annotation { "Feature Type Name" : "Feature", "Feature Type Description" : "" }
export const myFeature = defineFeature(function(context is Context, id is Id, definition is map)
    precondition{}
    {
        {
            var Q0;
            Q0=qCreatedBy(makeId("Top.planeOp"),FACE);
            var sketch = newSketch(context, id + "F0", { "sketchPlane" : qUnion([Q0])});
            skFitSpline(sketch, "E0", {"points": [v(57.34, 19.53) * mm, v(62.96, 14.6) * mm, v(65.23, 11.51) * mm, v(65.1, 6.78) * mm, v(63.4, 0.47) * mm, v(62.01, -6.29) * mm, v(62.2, -11.34) * mm, v(63.15, -16.32) * mm, v(62.96, -19.92) * mm, v(60.37, -26.55) * mm, v(57.34, -32.42) * mm, v(54.19, -36.9) * mm, v(51.85, -41.58) * mm, v(52.1, -45.11) * mm, v(51.79, -48.9) * mm, v(50.34, -52.24) * mm, v(46.61, -58.37) * mm, v(45.8, -61.9) * mm, v(44.84, -66.64) * mm, v(41.94, -71.18) * mm, v(36.83, -74.46) * mm, v(29.95, -76.36) * mm, v(24.45, -76.86) * mm, v(21.55, -76.17) * mm, v(19.21, -76.42) * mm, v(15.55, -77.12) * mm, v(11, -77.75) * mm, v(1.73, -77.87) * mm, v(-11.34, -73.7) * mm, v(-18.1, -68.47) * mm, v(-21.38, -62.85) * mm, v(-23.27, -59.63) * mm, v(-27.18, -57.42) * mm, v(-33.56, -52.18) * mm, v(-39.3, -44.92) * mm, v(-42.2, -35.52) * mm, v(-42.33, -35.45) * mm, v(-44.16, -36.02) * mm, v(-47.45, -35.2) * mm, v(-49.34, -32.42) * mm, v(-50.29, -26.49) * mm, v(-50.16, -22.57) * mm, v(-51.42, -17.4) * mm, v(-51.42, -15.44) * mm, v(-54.96, -10.26) * mm, v(-57.04, -5.85) * mm, v(-57.48, -1.17) * mm, v(-56.28, 4.5) * mm, v(-58.18, 7.85) * mm, v(-59.7, 15.05) * mm, v(-59.95, 22.3) * mm, v(-59.44, 34.18) * mm, v(-60.26, 40.87) * mm, v(-53.82, 51.28) * mm, v(-48.65, 57.6) * mm, v(-42.52, 64.22) * mm, v(-33.69, 70.73) * mm, v(-24.6, 75.27) * mm, v(-12.54, 78.55) * mm, v(1.8, 79.7) * mm, v(18.4, 77.92) * mm, v(39.16, 72.05) * mm, v(51.1, 64.67) * mm, v(56.9, 57.85) * mm, v(59.1, 48.95) * mm, v(59.3, 45.16) * mm, v(56.71, 42.07) * mm, v(54.31, 41.56) * mm, v(51.91, 41.69) * mm, v(52.1, 38.22) * mm, v(54.5, 31.84) * mm, v(56.02, 23.82) * mm, v(57.34, 19.53) * mm]});
            skSolve(sketch);
        }
        {
            var Q0;
            Q0 = qSketchRegion(id + "F0", true);
            extrude(context, id + "F1", {"entities" : qUnion([Q0]), "oppositeDirection" : true, "depth" : 6.35 * mm, "offsetDistance" : 25.4 * mm});
        }
        {
            var Q0;
            Q0=qCreatedBy(makeId("Top.planeOp"),FACE);
            var sketch = newSketch(context, id + "F2", { "sketchPlane" : qUnion([Q0])});
            skFitSpline(sketch, "E1", {"points": [v(-27.86, 37.73) * mm, v(-24.64, 35.15) * mm, v(-22.36, 34.68) * mm, v(-20.83, 36.15) * mm, v(-20.77, 37.61) * mm, v(-23.18, 41.13) * mm, v(-28.27, 46.87) * mm, v(-30.09, 48.4) * mm, v(-31.5, 48.74) * mm, v(-34.01, 46.75) * mm, v(-34.13, 44) * mm, v(-32.96, 42.65) * mm, v(-27.86, 37.73) * mm]});
            skFitSpline(sketch, "E2", {"points": [v(-23, 44.4) * mm, v(-21.71, 41.6) * mm, v(-20.01, 39.6) * mm, v(-17.73, 39.25) * mm, v(-15.62, 40.2) * mm, v(-15.15, 41.89) * mm, v(-16.67, 46.87) * mm, v(-18.78, 53.02) * mm, v(-20.36, 56.48) * mm, v(-22.47, 57.77) * mm, v(-26.46, 56.71) * mm, v(-27.92, 54.54) * mm, v(-27.69, 52.32) * mm, v(-26.16, 49.33) * mm, v(-23, 44.4) * mm]});
            skFitSpline(sketch, "E3", {"points": [v(-17.55, 55.3) * mm, v(-18.25, 57.77) * mm, v(-17.26, 59.46) * mm, v(-14.39, 60.4) * mm, v(-11.7, 59.35) * mm, v(-10.4, 56.6) * mm, v(-9.35, 50.91) * mm, v(-8.65, 45.81) * mm, v(-9.64, 43.12) * mm, v(-11.28, 42.7) * mm, v(-13.8, 43.88) * mm, v(-14.86, 46.17) * mm, v(-16.67, 51.97) * mm, v(-17.55, 55.3) * mm]});
            skFitSpline(sketch, "E4", {"points": [v(-7.36, 54.49) * mm, v(-6.89, 60.17) * mm, v(-6.36, 62.22) * mm, v(-4.84, 62.51) * mm, v(-3.08, 61.28) * mm, v(-1.32, 59.82) * mm, v(-0.33, 58.53) * mm, v(-0.5, 54.9) * mm, v(-0.21, 50.2) * mm, v(-0.15, 44.76) * mm, v(-0.1, 42.07) * mm, v(-0.62, 42.07) * mm, v(-4.02, 42.65) * mm, v(-6.07, 44.17) * mm, v(-6.71, 46.87) * mm, v(-7.12, 52.2) * mm, v(-7.36, 54.49) * mm]});
            skFitSpline(sketch, "E5", {"points": [v(2.2, 49.1) * mm, v(2.78, 53.14) * mm, v(2.95, 57.41) * mm, v(3.42, 59.82) * mm, v(4.53, 60.46) * mm, v(7.23, 59.58) * mm, v(9.1, 58.23) * mm, v(9.98, 55.36) * mm, v(9.63, 48.98) * mm, v(8.87, 42.53) * mm, v(8.46, 39.84) * mm, v(6.7, 39.49) * mm, v(3.71, 41.36) * mm, v(2.3, 43.88) * mm, v(2.2, 49.1) * mm]});
            skFitSpline(sketch, "E6", {"points": [v(12.38, 42.65) * mm, v(11.8, 49.8) * mm, v(12.15, 54.37) * mm, v(13.03, 56.95) * mm, v(15.43, 58.7) * mm, v(17.13, 58.3) * mm, v(18.42, 56.6) * mm, v(18.65, 54.6) * mm, v(18.65, 51.09) * mm, v(18.83, 47.63) * mm, v(18.89, 43.94) * mm, v(18.71, 40.13) * mm, v(18.65, 36.68) * mm, v(18.36, 35.27) * mm, v(17.42, 34.8) * mm, v(15.9, 35.04) * mm, v(13.38, 36.68) * mm, v(12.74, 38.55) * mm, v(12.38, 42.65) * mm]});
            skFitSpline(sketch, "E7", {"points": [v(25.62, 40.72) * mm, v(23.75, 37.79) * mm, v(22.4, 37.73) * mm, v(21.46, 40.72) * mm, v(20.88, 47.75) * mm, v(21.4, 54.3) * mm, v(22.87, 58.18) * mm, v(24.86, 59.23) * mm, v(27.44, 58.59) * mm, v(27.62, 56.83) * mm, v(27.67, 52.38) * mm, v(27.26, 46.87) * mm, v(26.97, 42.6) * mm, v(25.62, 40.72) * mm]});
            skFitSpline(sketch, "E8", {"points": [v(29.78, 51.44) * mm, v(29.55, 48.1) * mm, v(30.2, 45.35) * mm, v(31.83, 45.58) * mm, v(34.53, 46.4) * mm, v(35.35, 48.98) * mm, v(36.46, 53.78) * mm, v(36.99, 57) * mm, v(35.17, 58.64) * mm, v(33.06, 58.88) * mm, v(30.84, 57.82) * mm, v(30.37, 54.78) * mm, v(29.78, 51.44) * mm]});
            skFitSpline(sketch, "E9", {"points": [v(36.76, 48.28) * mm, v(38.51, 52.61) * mm, v(40.45, 55.72) * mm, v(42.09, 56.36) * mm, v(44.14, 55.19) * mm, v(44.25, 53.37) * mm, v(42.79, 49.74) * mm, v(40.45, 46.4) * mm, v(39.8, 44.88) * mm, v(37.87, 44.64) * mm, v(36.76, 48.28) * mm]});
            skFitSpline(sketch, "E10", {"points": [v(43.08, 42.89) * mm, v(42.26, 44.35) * mm, v(43.5, 46.87) * mm, v(45.95, 51.26) * mm, v(46.83, 53.55) * mm, v(49.23, 53.72) * mm, v(50.4, 51.09) * mm, v(49.94, 48.22) * mm, v(48.06, 45) * mm, v(45.66, 42.24) * mm, v(44.2, 41.6) * mm, v(43.08, 42.89) * mm]});
            skFitSpline(sketch, "E11", {"points": [v(-41.16, 32.22) * mm, v(-39.64, 35.33) * mm, v(-37.18, 37.09) * mm, v(-33.49, 36.91) * mm, v(-28.16, 36.09) * mm, v(-25.58, 34.86) * mm, v(-25.34, 33.16) * mm, v(-26.8, 29.76) * mm, v(-28.98, 28.7) * mm, v(-31.79, 28.94) * mm, v(-34.6, 29.41) * mm, v(-39.23, 28.53) * mm, v(-42.45, 28.24) * mm, v(-42.86, 28.83) * mm, v(-41.16, 32.22) * mm]});
            skFitSpline(sketch, "E12", {"points": [v(-44.03, 22.85) * mm, v(-45.5, 20.21) * mm, v(-45.03, 19.04) * mm, v(-42.68, 19.86) * mm, v(-38.88, 21.15) * mm, v(-31.67, 21.33) * mm, v(-29.1, 21.1) * mm, v(-27.22, 22.62) * mm, v(-27.63, 24.84) * mm, v(-28.33, 26.54) * mm, v(-30.38, 26.9) * mm, v(-36.77, 26.3) * mm, v(-41.98, 25.2) * mm, v(-44.03, 22.85) * mm]});
            skFitSpline(sketch, "E13", {"points": [v(-44.2, 16.11) * mm, v(-42.74, 18.1) * mm, v(-39.81, 18.98) * mm, v(-34.54, 19.16) * mm, v(-30.67, 19.28) * mm, v(-28.92, 19.45) * mm, v(-28.21, 17) * mm, v(-29.15, 13.89) * mm, v(-31.08, 13.07) * mm, v(-35.13, 13.48) * mm, v(-38.88, 13.77) * mm, v(-41.86, 13.18) * mm, v(-44.03, 13.07) * mm, v(-44.56, 14.12) * mm, v(-44.2, 16.11) * mm]});
            skFitSpline(sketch, "E14", {"points": [v(-40.75, 10.2) * mm, v(-36.42, 10.66) * mm, v(-32.37, 10.84) * mm, v(-28.92, 9.67) * mm, v(-28.39, 5.92) * mm, v(-30.73, 3.75) * mm, v(-34.37, 3.05) * mm, v(-38, 3.58) * mm, v(-42.04, 3.99) * mm, v(-46.02, 2.58) * mm, v(-46.96, -0.58) * mm, v(-45.73, -4.27) * mm, v(-43.27, -8.37) * mm, v(-41.63, -12.36) * mm, v(-40.46, -20.38) * mm, v(-40.46, -22.79) * mm, v(-39.81, -23.14) * mm, v(-37, -23.08) * mm, v(-33.84, -21.9) * mm, v(-31.79, -20.85) * mm, v(-30.8, -20.74) * mm, v(-30.44, -22.02) * mm, v(-31.73, -28.12) * mm, v(-31.2, -32.69) * mm, v(-29.39, -36.96) * mm, v(-25.52, -41.88) * mm, v(-21.3, -46.16) * mm, v(-20.13, -46.45) * mm, v(-19.9, -46.04) * mm, v(-20.13, -42.47) * mm, v(-19.72, -40.3) * mm, v(-18.02, -39.54) * mm, v(-15.56, -40.6) * mm, v(-14.27, -43.47) * mm, v(-13.28, -49.8) * mm, v(-12.1, -55.18) * mm, v(-9.06, -60.05) * mm, v(-6.07, -63.03) * mm, v(-1.8, -64.9) * mm, v(2.25, -66.14) * mm, v(8.28, -66.49) * mm, v(12.97, -65.55) * mm, v(15.43, -63.33) * mm, v(16.78, -59.58) * mm, v(18.95, -57.18) * mm, v(20.35, -56.41) * mm, v(22.58, -57.59) * mm, v(23.16, -60.7) * mm, v(22.75, -64.85) * mm, v(19.41, -69.24) * mm, v(15.6, -71.65) * mm, v(10.74, -72.52) * mm, v(4, -72.7) * mm, v(-1.91, -71.65) * mm, v(-7.24, -69.6) * mm, v(-12.92, -65.5) * mm, v(-15.74, -61.63) * mm, v(-17.84, -56.88) * mm, v(-19.08, -55.18) * mm, v(-23.23, -52.78) * mm, v(-28.27, -48.86) * mm, v(-32.78, -44.4) * mm, v(-35.95, -39.95) * mm, v(-37.76, -33.86) * mm, v(-37.82, -29.93) * mm, v(-38.11, -29.05) * mm, v(-39.05, -29.11) * mm, v(-41.4, -29.76) * mm, v(-43.91, -29.93) * mm, v(-45.5, -27.36) * mm, v(-45.61, -23.26) * mm, v(-46.43, -18.69) * mm, v(-46.32, -15.46) * mm, v(-47.6, -12.3) * mm, v(-50.18, -8.5) * mm, v(-52.53, -4.45) * mm, v(-52.12, 2.17) * mm, v(-49.36, 7.44) * mm, v(-48.02, 9.32) * mm, v(-40.75, 10.2) * mm]});
            skFitSpline(sketch, "E15", {"points": [v(-54.46, 14.7) * mm, v(-53.7, 10.49) * mm, v(-51.76, 8.85) * mm, v(-51.18, 9.02) * mm, v(-50.77, 10.25) * mm, v(-49.6, 11.07) * mm, v(-48.07, 12.25) * mm, v(-47.02, 15.35) * mm, v(-47.25, 17.87) * mm, v(-47.2, 20.86) * mm, v(-46.38, 23.03) * mm, v(-44.97, 24.9) * mm, v(-44.38, 29.59) * mm, v(-43.91, 32.99) * mm, v(-40.75, 36.97) * mm, v(-38.35, 39.2) * mm, v(-37.35, 41.07) * mm, v(-37, 45.81) * mm, v(-35.54, 48.98) * mm, v(-33.37, 50.91) * mm, v(-31.26, 52.61) * mm, v(-30.8, 55.13) * mm, v(-28.62, 57.53) * mm, v(-25.4, 59.35) * mm, v(-22.53, 59.76) * mm, v(-20.01, 60) * mm, v(-18.6, 60.99) * mm, v(-15.1, 62.1) * mm, v(-12.1, 61.98) * mm, v(-10.23, 62.1) * mm, v(-7.89, 63.57) * mm, v(-6.36, 64.21) * mm, v(-2.73, 64.03) * mm, v(-1.2, 63.21) * mm, v(1.6, 62.51) * mm, v(4.89, 62.92) * mm, v(7.64, 62.45) * mm, v(9.63, 60.28) * mm, v(11.5, 59.64) * mm, v(15.2, 60.28) * mm, v(17.19, 60.17) * mm, v(19.65, 59.7) * mm, v(22.23, 59.93) * mm, v(24.8, 61.05) * mm, v(27.56, 60.93) * mm, v(29.37, 60.28) * mm, v(32.07, 60.87) * mm, v(34.88, 61.1) * mm, v(38.34, 59.76) * mm, v(41.15, 58.88) * mm, v(44.72, 58.7) * mm, v(46.3, 57.36) * mm, v(47.48, 57) * mm, v(48.88, 58.35) * mm, v(49.12, 59) * mm, v(43.6, 63.21) * mm, v(35.17, 67.32) * mm, v(24.86, 70.6) * mm, v(13.61, 72.82) * mm, v(-0.04, 73.82) * mm, v(-11.64, 73.11) * mm, v(-21.36, 70.36) * mm, v(-31.2, 66.08) * mm, v(-39.11, 59.64) * mm, v(-44.5, 53.84) * mm, v(-51.3, 44.64) * mm, v(-54.23, 40.6) * mm, v(-54.81, 36.03) * mm, v(-54.4, 31.81) * mm, v(-54.64, 22.2) * mm, v(-54.46, 14.7) * mm]});
            skFitSpline(sketch, "E16", {"points": [v(51.75, 48.98) * mm, v(52.26, 51.54) * mm, v(51.3, 53.4) * mm, v(49.71, 54.74) * mm, v(49.32, 56.44) * mm, v(49.44, 57.7) * mm, v(50.82, 58.48) * mm, v(51.39, 58) * mm, v(51.75, 56.86) * mm, v(52.97, 55.37) * mm, v(53.4, 53.48) * mm, v(53.96, 51.54) * mm, v(54.83, 49.32) * mm, v(55.16, 48.34) * mm, v(53.9, 46.15) * mm, v(53.06, 45.73) * mm, v(51.69, 46.6) * mm, v(51.75, 48.98) * mm]});
            skFitSpline(sketch, "E17", {"points": [v(43.35, 20.43) * mm, v(42.79, 26.7) * mm, v(43.23, 33.08) * mm, v(43.01, 38.32) * mm, v(42.57, 40.53) * mm, v(43.04, 40.71) * mm, v(46.03, 39.22) * mm, v(48.46, 36.14) * mm, v(49.65, 31.87) * mm, v(50.27, 27.32) * mm, v(50.93, 21.3) * mm, v(53.3, 15.3) * mm, v(56.66, 12.55) * mm, v(59.1, 10.25) * mm, v(60.09, 8.32) * mm, v(59.34, 4.33) * mm, v(57.4, -2.18) * mm, v(56.54, -6.98) * mm, v(57.13, -12.18) * mm, v(57.88, -16.23) * mm, v(57.25, -21.6) * mm, v(55.91, -24.83) * mm, v(52.08, -30.97) * mm, v(48.71, -35.18) * mm, v(47.06, -37.73) * mm, v(46.19, -41.75) * mm, v(46.47, -45.84) * mm, v(45.7, -49.67) * mm, v(43.6, -54) * mm, v(40.95, -57.8) * mm, v(40.24, -60.73) * mm, v(39.58, -64.72) * mm, v(37.59, -68.11) * mm, v(33.26, -70.73) * mm, v(28.86, -72.14) * mm, v(25.4, -71.7) * mm, v(23.84, -70.36) * mm, v(23.66, -67.75) * mm, v(25.12, -65.25) * mm, v(26.96, -64.5) * mm, v(29.52, -63.82) * mm, v(32.13, -62.45) * mm, v(34.2, -59.08) * mm, v(35.25, -54.25) * mm, v(35.97, -51.79) * mm, v(39.08, -46.93) * mm, v(41.4, -43.25) * mm, v(41.67, -38.67) * mm, v(42.36, -33.22) * mm, v(44.32, -29.32) * mm, v(47.25, -25.3) * mm, v(49.96, -21.47) * mm, v(51.36, -18.5) * mm, v(50.9, -14.12) * mm, v(50.2, -10.88) * mm, v(50.18, -6.64) * mm, v(51.33, -1.69) * mm, v(52.08, 1) * mm, v(52.11, 4.23) * mm, v(51.64, 5.64) * mm, v(49.62, 5.64) * mm, v(47.62, 4.48) * mm, v(43.66, 3.95) * mm, v(37.5, 3.89) * mm, v(34.69, 3.14) * mm, v(33.23, 1.05) * mm, v(33.29, -1.7) * mm, v(34.47, -6.12) * mm, v(33.38, -11.13) * mm, v(31.2, -14.25) * mm, v(30.39, -17.74) * mm, v(30.7, -18.49) * mm, v(29.7, -19.64) * mm, v(27, -18.92) * mm, v(25.1, -16.68) * mm, v(25.18, -13.6) * mm, v(26.96, -9.6) * mm, v(28.33, -7.11) * mm, v(28.02, -3.87) * mm, v(26.62, -0.67) * mm, v(26.34, 3.04) * mm, v(28.24, 7.25) * mm, v(30.86, 9.21) * mm, v(34.94, 10.37) * mm, v(40.83, 10.71) * mm, v(45.63, 11.15) * mm, v(47.16, 11.65) * mm, v(47.1, 12.02) * mm, v(46.16, 13.2) * mm, v(44.26, 16.63) * mm, v(43.35, 20.43) * mm]});
            skFitSpline(sketch, "E18", {"points": [v(-7.93, 9.02) * mm, v(-13.72, 11.66) * mm, v(-19.88, 12.99) * mm, v(-22.07, 13.58) * mm, v(-22.18, 14.66) * mm, v(-20.72, 15.85) * mm, v(-20.07, 16.74) * mm, v(-19.99, 17.28) * mm, v(-19.02, 17.83) * mm, v(-17.9, 17.88) * mm, v(-17.23, 18.77) * mm, v(-16.67, 19.16) * mm, v(-15.28, 19.72) * mm, v(-14.42, 19.61) * mm, v(-13.8, 20.43) * mm, v(-12.54, 20.8) * mm, v(-10.86, 20) * mm, v(-9.26, 19.16) * mm, v(-7.58, 19.16) * mm, v(-6.12, 18.53) * mm, v(-5.15, 16.72) * mm, v(-4.37, 14.83) * mm, v(-2.53, 13.13) * mm, v(2.1, 10.78) * mm, v(7.65, 8.21) * mm, v(12.5, 6.24) * mm, v(15.12, 5.1) * mm, v(15.8, 3.65) * mm, v(15.17, 1.83) * mm, v(12.79, 0.67) * mm, v(9.19, 0.8) * mm, v(6, 2.3) * mm, v(1.2, 4.56) * mm, v(-2.56, 6.37) * mm, v(-7.93, 9.02) * mm]});
            skFitSpline(sketch, "E19", {"points": [v(-35.34, -12.25) * mm, v(-35.7, -11.63) * mm, v(-35.05, -10.48) * mm, v(-33, -9.39) * mm, v(-31.58, -8.72) * mm, v(-31.07, -6.58) * mm, v(-32.14, -3.88) * mm, v(-34.13, -1.88) * mm, v(-37.21, -1.02) * mm, v(-39.75, -1.84) * mm, v(-41.48, -3.46) * mm, v(-41.56, -4.67) * mm, v(-40.15, -5.58) * mm, v(-38.57, -7.11) * mm, v(-38.1, -9.26) * mm, v(-37.84, -11.51) * mm, v(-37.27, -13.32) * mm, v(-36.61, -14.67) * mm, v(-35.2, -15.37) * mm, v(-33.9, -15.09) * mm, v(-33.43, -13.73) * mm, v(-33.52, -13.26) * mm, v(-34.74, -13.2) * mm, v(-35.34, -12.25) * mm]});
            skFitSpline(sketch, "E20", {"points": [v(-2.61, -52.95) * mm, v(-4.22, -51.02) * mm, v(-4.14, -47.78) * mm, v(-1.95, -43.74) * mm, v(-0.65, -42.1) * mm, v(3.08, -39.14) * mm, v(9.4, -36) * mm, v(14.77, -34.51) * mm, v(21.62, -34.02) * mm, v(27.41, -34.47) * mm, v(32.47, -36.18) * mm, v(34.3, -37.57) * mm, v(37.16, -41.42) * mm, v(38.49, -44.14) * mm, v(37.91, -45.38) * mm, v(36.2, -44.8) * mm, v(34.11, -43.25) * mm, v(29.58, -41.35) * mm, v(23.73, -40.75) * mm, v(17.4, -40.72) * mm, v(11.19, -42.26) * mm, v(8.14, -44.14) * mm, v(7.26, -45.4) * mm, v(7.38, -45.99) * mm, v(8.72, -45.78) * mm, v(12.3, -44.9) * mm, v(15.04, -44.39) * mm, v(15.48, -44.6) * mm, v(14.75, -46.47) * mm, v(11.07, -49.49) * mm, v(6.61, -52.65) * mm, v(2.76, -53.84) * mm, v(-0.24, -54.08) * mm, v(-2.61, -52.95) * mm]});
            skFitSpline(sketch, "E21", {"points": [v(41.47, -5.84) * mm, v(40.72, -3.6) * mm, v(41.67, -1.3) * mm, v(43.98, -0.51) * mm, v(46.24, -1.16) * mm, v(47.69, -2.63) * mm, v(47.96, -4.4) * mm, v(46.72, -6.12) * mm, v(44.33, -7.11) * mm, v(41.67, -6.12) * mm, v(41.47, -5.84) * mm]});
            skFitSpline(sketch, "E22", {"points": [v(-1.93, -8.73) * mm, v(-6.41, -9.22) * mm, v(-10.4, -8.35) * mm, v(-12.92, -5.72) * mm, v(-13.58, -3.55) * mm, v(-12.08, -2.9) * mm, v(-7.63, -2.94) * mm, v(-0.64, -2.8) * mm, v(4.31, -2.9) * mm, v(7.56, -3.1) * mm, v(8.91, -4.3) * mm, v(10.8, -6.87) * mm, v(11.13, -8.19) * mm, v(9.63, -8.81) * mm, v(6.3, -8.44) * mm, v(-1.93, -8.73) * mm]});
            skFitSpline(sketch, "E23", {"points": [v(-4.1, -27.42) * mm, v(-7.44, -30.79) * mm, v(-8.65, -32.21) * mm, v(-9.97, -32.48) * mm, v(-10.76, -30.1) * mm, v(-10.84, -27.5) * mm, v(-10.04, -25.8) * mm, v(-7.97, -23.69) * mm, v(-5.04, -21.1) * mm, v(-1.6, -18.52) * mm, v(1.35, -16.64) * mm, v(3.97, -14.84) * mm, v(7, -13.42) * mm, v(10.76, -12.25) * mm, v(14.35, -11.35) * mm, v(18.84, -10.78) * mm, v(19.66, -10.96) * mm, v(19.35, -12.25) * mm, v(18.02, -13.95) * mm, v(17.46, -16.44) * mm, v(17.83, -18.42) * mm, v(18.9, -19.5) * mm, v(21.22, -19.72) * mm, v(22.9, -20.62) * mm, v(24.53, -22.02) * mm, v(26.4, -23.72) * mm, v(27.83, -23.86) * mm, v(29.5, -22.72) * mm, v(31.42, -21.2) * mm, v(32.23, -20.06) * mm, v(33.64, -19.26) * mm, v(35.36, -18.43) * mm, v(37.5, -16.97) * mm, v(38.64, -15.67) * mm, v(39.27, -14.21) * mm, v(39.62, -12.85) * mm, v(40.56, -12.85) * mm, v(41.41, -14.14) * mm, v(42.27, -16.31) * mm, v(42.41, -19.15) * mm, v(41.67, -21.76) * mm, v(39.16, -24.15) * mm, v(36.17, -25.58) * mm, v(33.89, -26.86) * mm, v(31.74, -28.87) * mm, v(29.65, -30.88) * mm, v(26.73, -31.85) * mm, v(23.97, -30.65) * mm, v(20.96, -28.01) * mm, v(18.97, -25.99) * mm, v(18.2, -25.45) * mm, v(15.1, -24.86) * mm, v(11.87, -23.67) * mm, v(11, -21.59) * mm, v(10.44, -19.49) * mm, v(10.1, -18.92) * mm, v(8.77, -19.32) * mm, v(5.55, -20.7) * mm, v(1.98, -22.75) * mm, v(-1.55, -25.02) * mm, v(-3.5, -26.74) * mm, v(-4.1, -27.42) * mm]});
            skSolve(sketch);
        }
        {
            var Q0;
            Q0 = qSketchRegion(id + "F2", true);
            extrude(context, id + "F3", {"entities" : qUnion([Q0]), "operationType" : NewBodyOperationType.ADD, "depth" : 6.35 * mm, "offsetDistance" : 25.4 * mm});
        }
        {
            var Q0;
            Q0=makeQuery(id+"F1.opExtrude","CAP_FACE",FACE,{"disambiguationData":[OSD([sQuery(id+"F0.wireOp",EDGE,"E0")])],"isStart":false});
            var sketch = newSketch(context, id + "F4", { "sketchPlane" : qUnion([Q0])});
            skText(sketch, "E24", { "text": "Riley Frisell", "fontName": "Arimo-Bold.ttf"});
            const initialGuessF4  = {"E24": [0.0029, 0.06982, -0.76604, -0.64279, 0.00635]};
            skSetInitialGuess(sketch, initialGuessF4);
            skSolve(sketch);
        }
        {
            var Q0;
            Q0 = qSketchRegion(id + "F4", true);
            extrude(context, id + "F5", {"entities" : qUnion([Q0]), "operationType" : NewBodyOperationType.REMOVE, "oppositeDirection" : true, "depth" : 3.17 * mm, "offsetDistance" : 25.4 * mm});
        }
    });